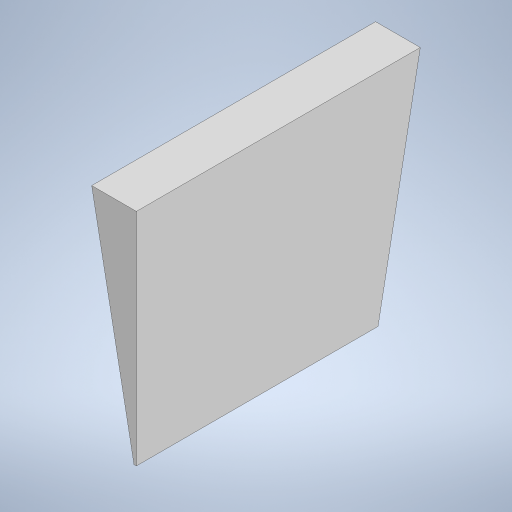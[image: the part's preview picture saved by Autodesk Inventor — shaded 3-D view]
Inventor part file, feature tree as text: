
AUTODESK INVENTOR PART (.ipt)
format: ipt  version: 2024.2 (Build 282272000, 272)  size: 194,048 bytes
history: native  units: in
note: dims shown in document units (in); Inventor stores cm internally (conversion verified against a paired STEP export)
features: extrude x1, sketch x1
ambient origin geometry x8: Origin, YZ Plane, XZ Plane, XY Plane, X Axis, Y Axis, Z Axis, Center Point
bodies: Solid1 (feature_tree)
feature tree (2):
  extrude  "Extrusion1"  Depth=1.0in
  sketch  "Sketch1"  dims[d0=0.01in d1=1.0in d2=1.0in d3=0.0344in]
